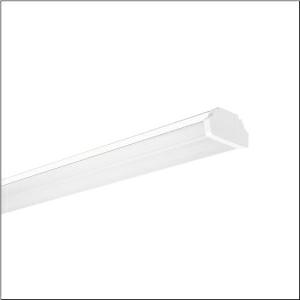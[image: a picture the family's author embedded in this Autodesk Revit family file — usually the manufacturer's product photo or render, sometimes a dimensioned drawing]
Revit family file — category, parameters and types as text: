
# Revit family: dus_31_gen_2_53bd811dv4a5c2_c54e
name_source: partatom
category: Lighting Fixtures
units: mm (PartAtom-declared; Revit-internal decimal feet)

## family parameters
Cut with Voids When Loaded = No
Host = Face
Light Source = No
Part Type = Normal
Room Calculation Point = No
Round Connector Dimension = Use Diameter
Shared = No

## types (1)
- --- (1 x LED, 10860 lm, 61.4 W, 4000K)
    Apparent Load = 61 VA
    CIE Flux Codes = 50 78 94 90 100
    Color Rendering = 80
    Color Temperature = 4000K
    Default Elevation = 1800 mm
    Description = DUS 31 Gen.2, luminaire insert, of sheet steel, coil coated, white, length: 1.535mm, width: 81mm, height: 90mm, 5x system unit, system units: 307mm, LED rated luminous flux: 10.860lm, light colour: 840, SDCM (Standard Deviation of Colour Matching)MacAdam ≤ 3 SDCM (initial), control gear: DALI 2, control gear: ECG DALI, with plug, 5-pole, with phase selection, mains connection: 220..240V, AC, 50/60Hz, rated input power: 61W, through-wiring accessed according to module size, primary optical cover: cover, of PMMA, light emission: direct distribution, primary light characteristic: symmetric, protection rating (complete): IP20, protection rating (LED compartment): IP50, insulation class (complete): insulation class I (protective earthing), certification: CE, ENEC, VDE, UKCA, impact resistance: IK03, permissible ambient temperature for indoor applications: -25..+35°C, corresponds to IFS (International Featured Standards) requirements for safety and quality in the food industry, reducing of maximum allowable ambient temperature of 5°C with ceiling mounting, packaging unit: 1 piece
    Height = 95 mm
    Lamp = 1 x LED
    Lamp Light Flux = 10860 lm
    Lamp Power = 61.4 W
    Lamp count = 1
    Length = 1535 mm
    Luminous efficacy = 177 lm/W
    Manufacturer = Siteco
    ModVariant = No
    Model = 53BD811DV4A5C2
    Mounting Place = Ceiling
    Mounting Type = Pendant
    Number of Poles = 1
    OnlyDefault = Yes
    Power Factor = 1
    Product Name = DUS 31 Gen.2
    Product group = luminaire insert | ceiling pendant
    ProductGroupID = 901
    Protection Class = Protection class I
    Protection Degree = IP 20
    RLX_Detail_Level = 1
    RLX_Emergency_Light_Flux = 0 lm
    RLX_Emergency_Type = 0
    RLX_Emergency_Type_DB = No
    RlxData = <blob elided: 32273 chars, md5=98857fec>
    Socket = socket
    Standby Power = 0 W
    System Light Flux = 10860 lm
    System Power = 61 W
    Type Comments = factory setting: luminous flux: 100 % | dim-lin: 254 | 418 mA
    Type Image = l_1319596.jpg
    URL = http://relux.com
    VarID = @adj_051783
    Voltage = 0 V
    Weight = 0.00 kg
    Width = 81 mm

## geometry (parser evidence)
native form markers: Blend x4, Sweep x13
no freeform markers — native parametric forms only
